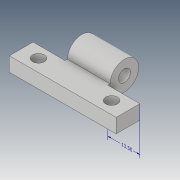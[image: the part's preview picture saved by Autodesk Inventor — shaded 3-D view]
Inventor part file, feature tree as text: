
AUTODESK INVENTOR PART (.ipt)
format: ipt  version: 2019 (Build 230136000, 136)  size: 150,528 bytes
history: native  units: mm
features: extrude x4, sketch x4, other x2, move_body x2, fillet x1, plane x1, direct_edit x1
ambient origin geometry x8: Origin, YZ Plane, XZ Plane, XY Plane, X Axis, Y Axis, Z Axis, Center Point
bodies: Solid1 (feature_tree)
feature tree (15):
  other  "Annotations"
  extrude  "Extrusion1"  Depth=45.0mm
  sketch  "Sketch4"  dims[d5=5.0mm d6=5.0mm d7=11.0mm]
  extrude  "Extrusion4"  Depth=5.0mm
  fillet  "Fillet1"  Radius=11.0mm
  extrude  "Extrusion5"  Depth=23.0mm
  plane  "Work Plane1"
  extrude  "Extrusion6"  Depth=12.0mm
  direct_edit  "Direct Edit1"
  sketch  "Sketch1"  dims[d0=6.0mm d1=0.0mm d4=45.0mm]
  sketch  "Sketch5"  dims[d8=11.0mm d9=23.0mm]
  sketch  "Sketch6"  dims[d10=10.0mm d20=12.0mm d21=0.0mm d24=3.0mm d25=0.0mm d26=12.0mm d27=5.0mm d28=3.0mm d29=0.0mm d33=5.0mm d34=5.0mm d35=17.8mm d36=7.0mm d37=17.8mm d38=7.1mm d39=30.8mm d40=7.1mm d41=3.0mm d42=0.0mm d46=0.0mm d47=0.0mm d48=-2.5mm d49=0.0mm d50=0.0mm d51=-2.5mm d43=0.0mm d44=10.0mm d45=13.5mm]
  move_body  "Move1"
  move_body  "Move2"
  other  "Linear Dimension 1"
